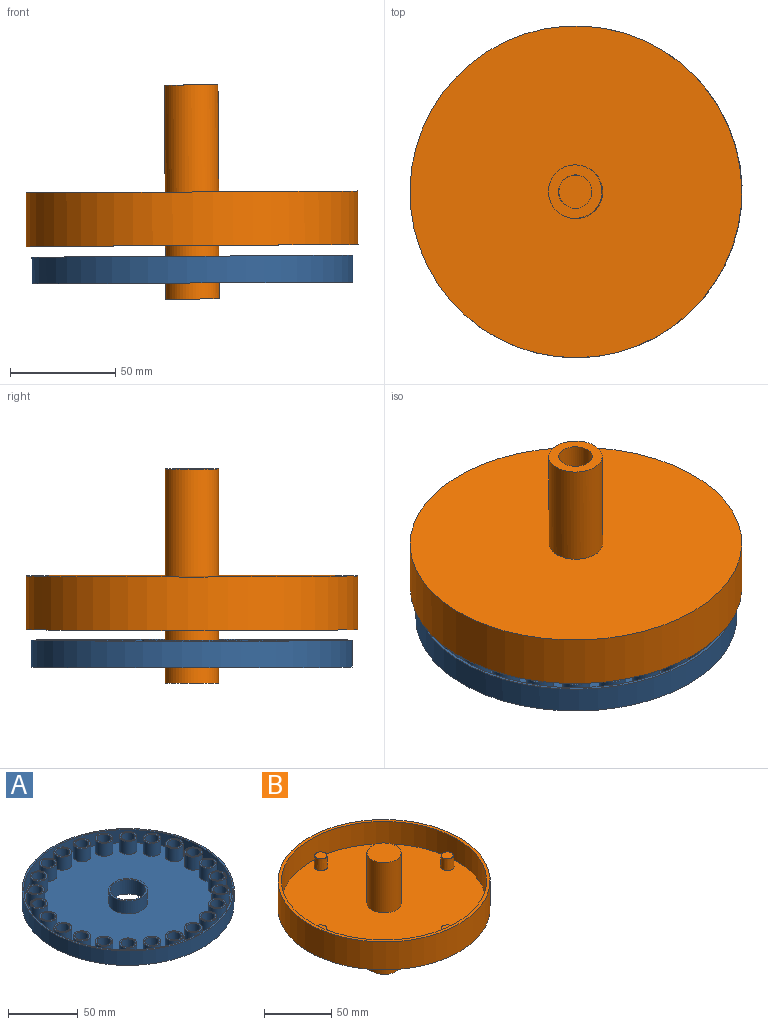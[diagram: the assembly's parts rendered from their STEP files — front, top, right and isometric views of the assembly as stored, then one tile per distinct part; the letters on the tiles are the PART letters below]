
ASSEMBLY  parts=2 mates=1
PART A: 80 faces, bbox 152.4x152.4x12.7 mm
  f0: plane 12.7x12.7mm, normal (0,0,1), area 45.6mm2, adj f49,f77
  f1: plane 12.7x12.7mm, normal (0,0,1), area 45.6mm2, adj f48,f76
  f2: plane 12.7x12.7mm, normal (0,0,1), area 45.6mm2, adj f47,f75
  f3: plane 12.7x12.7mm, normal (0,0,1), area 45.6mm2, adj f46,f74
  f4: plane 12.7x12.7mm, normal (0,0,1), area 45.6mm2, adj f45,f73
  f5: plane 12.7x12.7mm, normal (0,0,1), area 45.6mm2, adj f44,f72
  f6: plane 12.7x12.7mm, normal (0,0,1), area 45.6mm2, adj f43,f71
  f7: plane 12.7x12.7mm, normal (0,0,1), area 45.6mm2, adj f42,f70
  f8: plane 12.7x12.7mm, normal (0,0,1), area 45.6mm2, adj f41,f69
  f9: plane 12.7x12.7mm, normal (0,0,1), area 45.6mm2, adj f40,f68
  f10: plane 12.7x12.7mm, normal (0,0,1), area 45.6mm2, adj f39,f67
  f11: plane 12.7x12.7mm, normal (0,0,1), area 45.6mm2, adj f38,f66
  f12: plane 12.7x12.7mm, normal (0,0,1), area 45.6mm2, adj f37,f65
  f13: plane 12.7x12.7mm, normal (0,0,1), area 45.6mm2, adj f36,f64
  f14: plane 12.7x12.7mm, normal (0,0,1), area 45.6mm2, adj f35,f63
  f15: plane 12.7x12.7mm, normal (0,0,1), area 45.6mm2, adj f34,f62
  f16: plane 12.7x12.7mm, normal (0,0,1), area 45.6mm2, adj f33,f61
  f17: plane 12.7x12.7mm, normal (0,0,1), area 45.6mm2, adj f32,f60
  f18: plane 12.7x12.7mm, normal (0,0,1), area 45.6mm2, adj f31,f59
  f19: plane 12.7x12.7mm, normal (0,0,1), area 45.6mm2, adj f30,f58
  f20: plane 12.7x12.7mm, normal (0,0,1), area 45.6mm2, adj f29,f57
  f21: plane 12.7x12.7mm, normal (0,0,1), area 45.6mm2, adj f28,f56
  f22: plane 12.7x12.7mm, normal (0,0,1), area 45.6mm2, adj f27,f55
  f23: plane 12.7x12.7mm, normal (0,0,1), area 45.6mm2, adj f26,f54
  f24: plane 27.94x27.94mm, normal (0,0,1), area 106.4mm2, adj f25,f53
  f25: cylinder r=12.7mm len=25.4mm, axis (0,0,-1), area 1013.4mm2, adj f24,f52
  f26: cylinder r=5.08mm len=12.7mm, axis (0,0,-1), area 405.4mm2, adj f23,f52
  f27: cylinder r=5.08mm len=12.7mm, axis (0,0,-1), area 405.4mm2, adj f22,f52
  f28: cylinder r=5.08mm len=12.7mm, axis (0,0,-1), area 405.4mm2, adj f21,f52
  f29: cylinder r=5.08mm len=12.7mm, axis (0,0,-1), area 405.4mm2, adj f20,f52
  f30: cylinder r=5.08mm len=12.7mm, axis (0,0,-1), area 405.4mm2, adj f19,f52
  f31: cylinder r=5.08mm len=12.7mm, axis (0,0,-1), area 405.4mm2, adj f18,f52
  f32: cylinder r=5.08mm len=12.7mm, axis (0,0,-1), area 405.4mm2, adj f17,f52
  f33: cylinder r=5.08mm len=12.7mm, axis (0,0,-1), area 405.4mm2, adj f16,f52
  f34: cylinder r=5.08mm len=12.7mm, axis (0,0,-1), area 405.4mm2, adj f15,f52
  f35: cylinder r=5.08mm len=12.7mm, axis (0,0,-1), area 405.4mm2, adj f14,f52
  f36: cylinder r=5.08mm len=12.7mm, axis (0,0,-1), area 405.4mm2, adj f13,f52
  f37: cylinder r=5.08mm len=12.7mm, axis (0,0,-1), area 405.4mm2, adj f12,f52
  f38: cylinder r=5.08mm len=12.7mm, axis (0,0,-1), area 405.4mm2, adj f11,f52
  f39: cylinder r=5.08mm len=12.7mm, axis (0,0,-1), area 405.4mm2, adj f10,f52
  f40: cylinder r=5.08mm len=12.7mm, axis (0,0,-1), area 405.4mm2, adj f9,f52
  f41: cylinder r=5.08mm len=12.7mm, axis (0,0,-1), area 405.4mm2, adj f8,f52
  f42: cylinder r=5.08mm len=12.7mm, axis (0,0,-1), area 405.4mm2, adj f7,f52
  f43: cylinder r=5.08mm len=12.7mm, axis (0,0,-1), area 405.4mm2, adj f6,f52
  f44: cylinder r=5.08mm len=12.7mm, axis (0,0,-1), area 405.4mm2, adj f5,f52
  f45: cylinder r=5.08mm len=12.7mm, axis (0,0,-1), area 405.4mm2, adj f4,f52
  f46: cylinder r=5.08mm len=12.7mm, axis (0,0,-1), area 405.4mm2, adj f3,f52
  f47: cylinder r=5.08mm len=12.7mm, axis (0,0,-1), area 405.4mm2, adj f2,f52
  f48: cylinder r=5.08mm len=12.7mm, axis (0,0,-1), area 405.4mm2, adj f1,f52
  f49: cylinder r=5.08mm len=12.7mm, axis (0,0,-1), area 405.4mm2, adj f0,f52
  f50: cylinder r=76.2mm len=152.4mm, axis (0,0,-1), area 6080.5mm2, adj f51,f52
  f51: plane 152.4x152.4mm, normal (0,0,1), area 603mm2, adj f50,f78
  f52: plane 152.4x152.4mm, normal (0,0,-1), area 15789mm2, adj f25,f26,f27,f28,f29,f30,f31,f32
  f53: cylinder r=13.97mm len=27.94mm, axis (0,0,-1), area 1003.3mm2, adj f24,f79
  f54: cylinder r=6.35mm len=12.7mm, axis (0,0,-1), area 456mm2, adj f23,f79
  f55: cylinder r=6.35mm len=12.7mm, axis (0,0,-1), area 456mm2, adj f22,f79
  f56: cylinder r=6.35mm len=12.7mm, axis (0,0,-1), area 456mm2, adj f21,f79
  f57: cylinder r=6.35mm len=12.7mm, axis (0,0,-1), area 456mm2, adj f20,f79
  f58: cylinder r=6.35mm len=12.7mm, axis (0,0,-1), area 456mm2, adj f19,f79
  f59: cylinder r=6.35mm len=12.7mm, axis (0,0,-1), area 456mm2, adj f18,f79
  f60: cylinder r=6.35mm len=12.7mm, axis (0,0,-1), area 456mm2, adj f17,f79
  f61: cylinder r=6.35mm len=12.7mm, axis (0,0,-1), area 456mm2, adj f16,f79
  f62: cylinder r=6.35mm len=12.7mm, axis (0,0,-1), area 456mm2, adj f15,f79
  f63: cylinder r=6.35mm len=12.7mm, axis (0,0,-1), area 456mm2, adj f14,f79
  f64: cylinder r=6.35mm len=12.7mm, axis (0,0,-1), area 456mm2, adj f13,f79
  f65: cylinder r=6.35mm len=12.7mm, axis (0,0,-1), area 456mm2, adj f12,f79
  f66: cylinder r=6.35mm len=12.7mm, axis (0,0,-1), area 456mm2, adj f11,f79
  f67: cylinder r=6.35mm len=12.7mm, axis (0,0,-1), area 456mm2, adj f10,f79
  f68: cylinder r=6.35mm len=12.7mm, axis (0,0,-1), area 456mm2, adj f9,f79
  f69: cylinder r=6.35mm len=12.7mm, axis (0,0,-1), area 456mm2, adj f8,f79
  f70: cylinder r=6.35mm len=12.7mm, axis (0,0,-1), area 456mm2, adj f7,f79
  f71: cylinder r=6.35mm len=12.7mm, axis (0,0,-1), area 456mm2, adj f6,f79
  f72: cylinder r=6.35mm len=12.7mm, axis (0,0,-1), area 456mm2, adj f5,f79
  f73: cylinder r=6.35mm len=12.7mm, axis (0,0,-1), area 456mm2, adj f4,f79
  f74: cylinder r=6.35mm len=12.7mm, axis (0,0,-1), area 456mm2, adj f3,f79
  f75: cylinder r=6.35mm len=12.7mm, axis (0,0,-1), area 456mm2, adj f2,f79
  f76: cylinder r=6.35mm len=12.7mm, axis (0,0,-1), area 456mm2, adj f1,f79
  f77: cylinder r=6.35mm len=12.7mm, axis (0,0,-1), area 456mm2, adj f0,f79
  f78: cylinder r=74.93mm len=149.86mm, axis (0,0,-1), area 5381.2mm2, adj f51,f79
  f79: plane 149.86x149.86mm, normal (0,0,1), area 13985.1mm2, adj f53,f54,f55,f56,f57,f58,f59,f60
PART B: 19 faces, bbox 157.5x157.5x101.6 mm
  f0: plane 152.4x152.4mm, normal (0,0,1), area 17410.5mm2, adj f2,f4,f6,f8,f10,f15
  f1: plane 157.48x157.48mm, normal (0,0,-1), area 18971.1mm2, adj f11,f14
  f2: cone r=5.08mm half-angle=3deg, axis (0,0,-1), area 307.7mm2, adj f0,f3
  f3: plane 9.1x9.1mm, normal (0,0,1), area 65mm2, adj f2
  f4: cone r=5.08mm half-angle=3deg, axis (0,0,-1), area 307.7mm2, adj f0,f5
  f5: plane 9.1x9.1mm, normal (0,0,1), area 65mm2, adj f4
  f6: cone r=5.08mm half-angle=3deg, axis (0,0,-1), area 307.7mm2, adj f0,f7
  f7: plane 9.1x9.1mm, normal (0,0,1), area 65mm2, adj f6
  f8: cone r=5.08mm half-angle=3deg, axis (0,0,-1), area 307.7mm2, adj f0,f9
  f9: plane 9.1x9.1mm, normal (0,0,1), area 65mm2, adj f8
  f10: cylinder r=76.2mm len=152.4mm, axis (0,0,-1), area 9728.8mm2, adj f0,f12
  f11: cylinder r=78.74mm len=157.48mm, axis (0,0,-1), area 12566.3mm2, adj f1,f12
  f12: plane 157.48x157.48mm, normal (0,0,1), area 1236.4mm2, adj f10,f11
  f13: plane 25.4x25.4mm, normal (0,0,-1), area 308.8mm2, adj f14,f17
  f14: cylinder r=12.7mm len=50.8mm, axis (0,0,-1), area 4053.7mm2, adj f1,f13
  f15: cylinder r=12.7mm len=45.72mm, axis (0,0,-1), area 3648.3mm2, adj f0,f16
  f16: plane 25.4x25.4mm, normal (0,0,1), area 506.7mm2, adj f15
  f17: cylinder r=7.94mm len=25.4mm, axis (0,0,-1), area 1266.8mm2, adj f13,f18
  f18: plane 15.88x15.88mm, normal (0,0,-1), area 197.9mm2, adj f17
PLACE A rot(axis=(0,-1,0),0.3deg) t=(-8.82,-17.35,43.05)mm fixed
PLACE B rot(axis=(1,0.02,0),180deg) t=(-9.08,-17.35,86.23)mm
MATE cylindrical B.f14 <-> A.f25  axis (-0.01,0,1) through (-9.05,-17.35,81.15)mm
